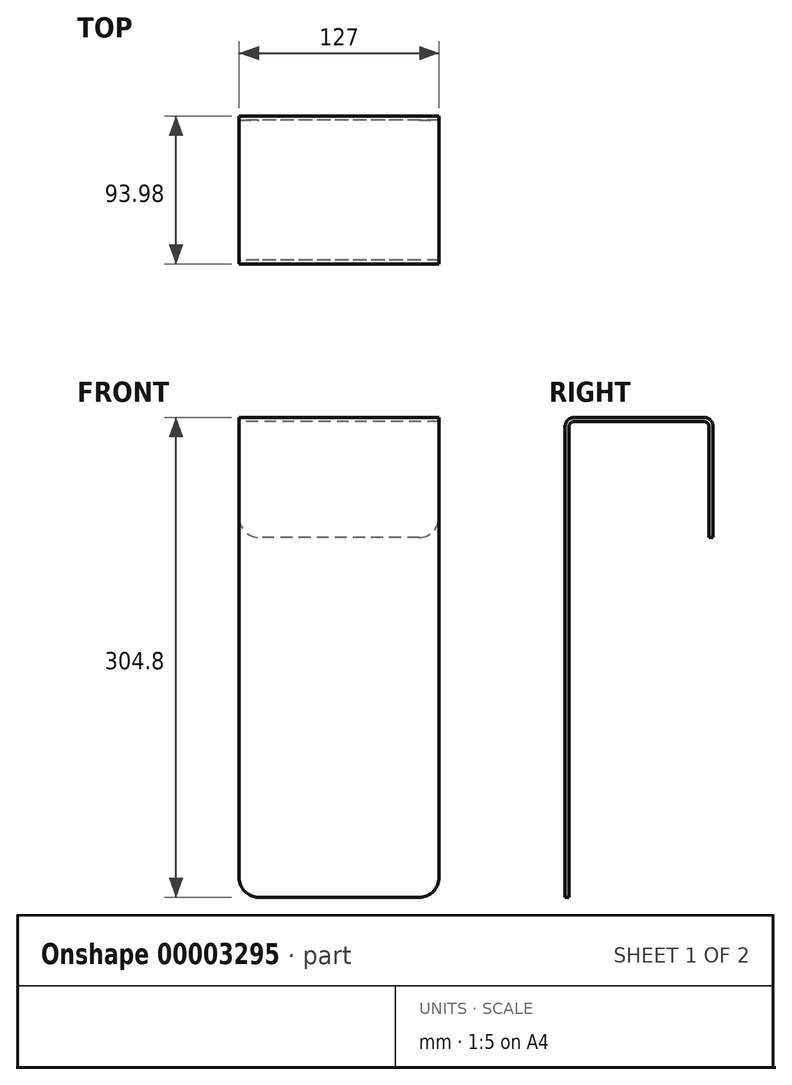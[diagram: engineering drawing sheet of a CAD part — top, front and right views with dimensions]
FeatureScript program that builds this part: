
annotation { "Feature Type Name" : "Feature", "Feature Type Description" : "" }
export const myFeature = defineFeature(function(context is Context, id is Id, definition is map)
    precondition{}
    {
        {
            var Q0;
            Q0=qCreatedBy(makeId("Right.planeOp"),FACE);
            var sketch = newSketch(context, id + "F0", { "sketchPlane" : qUnion([Q0])});
            skLineSegment(sketch, "E0", {"start": v(0, 0) * mm, "end": v(-2.54, 0) * mm});
            skLineSegment(sketch, "E1", {"start": v(-2.54, 0) * mm, "end": v(-2.54, 299.09) * mm});
            skLineSegment(sketch, "E2", {"start": v(3.17, 304.8) * mm, "end": v(85.72, 304.8) * mm});
            skLineSegment(sketch, "E3", {"start": v(91.44, 299.09) * mm, "end": v(91.44, 228.6) * mm});
            skLineSegment(sketch, "E4", {"start": v(91.44, 228.6) * mm, "end": v(88.9, 228.6) * mm});
            skLineSegment(sketch, "E5", {"start": v(88.9, 228.6) * mm, "end": v(88.9, 299.09) * mm});
            skLineSegment(sketch, "E6", {"start": v(85.72, 302.26) * mm, "end": v(3.17, 302.26) * mm});
            skLineSegment(sketch, "E7", {"start": v(0, 299.09) * mm, "end": v(0, 0) * mm});
            skPoint(sketch, "E8.visualSharp", {"position": v(88.9, 302.26) * mm});
            skArc(sketch, "E8.filletArc", {"start": v(88.9, 299.09) * mm, "mid": v(87.97, 301.33) * mm, "end": v(85.72, 302.26) * mm});
            skPoint(sketch, "E9.visualSharp", {"position": v(0, 302.26) * mm});
            skArc(sketch, "E9.filletArc", {"start": v(3.17, 302.26) * mm, "mid": v(0.93, 301.33) * mm, "end": v(0, 299.09) * mm});
            skPoint(sketch, "E10.visualSharp", {"position": v(91.44, 304.8) * mm});
            skArc(sketch, "E10.filletArc", {"start": v(91.44, 299.09) * mm, "mid": v(89.77, 303.13) * mm, "end": v(85.72, 304.8) * mm});
            skPoint(sketch, "E11.visualSharp", {"position": v(-2.54, 304.8) * mm});
            skArc(sketch, "E11.filletArc", {"start": v(3.17, 304.8) * mm, "mid": v(-0.87, 303.13) * mm, "end": v(-2.54, 299.09) * mm});
            skSolve(sketch);
        }
        {
            var Q0;
            Q0=makeQuery(id+"F0.imprint","IMPRINT",FACE,{"disambiguationData":[TD([[makeQuery(id+"F0.imprint","IMPRINT",EDGE,{"derivedFrom":sQuery(id+"F0.wireOp",EDGE,"E0")}),-1.0]])]});
            extrude(context, id + "F1", {"entities" : qUnion([Q0]), "endBound" : BoundingType.SYMMETRIC, "depth" : 127 * mm});
        }
        {
            var Q0;
            Q0=makeQuery(id+"F1.opExtrude","CAP_EDGE",EDGE,{"disambiguationData":[OSD([sQuery(id+"F0.wireOp",EDGE,"E0")])],"isStart":false});
            var Q1;
            Q1=makeQuery(id+"F1.opExtrude","CAP_EDGE",EDGE,{"disambiguationData":[OSD([sQuery(id+"F0.wireOp",EDGE,"E0")])],"isStart":true});
            var Q2;
            Q2=makeQuery(id+"F1.opExtrude","CAP_EDGE",EDGE,{"disambiguationData":[OSD([sQuery(id+"F0.wireOp",EDGE,"E4")])],"isStart":false});
            var Q3;
            Q3=makeQuery(id+"F1.opExtrude","CAP_EDGE",EDGE,{"disambiguationData":[OSD([sQuery(id+"F0.wireOp",EDGE,"E4")])],"isStart":true});
            fillet(context, id + "F2", {"entities" : qUnion([Q0, Q1, Q2, Q3]), "radius" : 12.7 * mm, "tangentPropagation" : true, "allowEdgeOverflow" : false});
        }
    });
